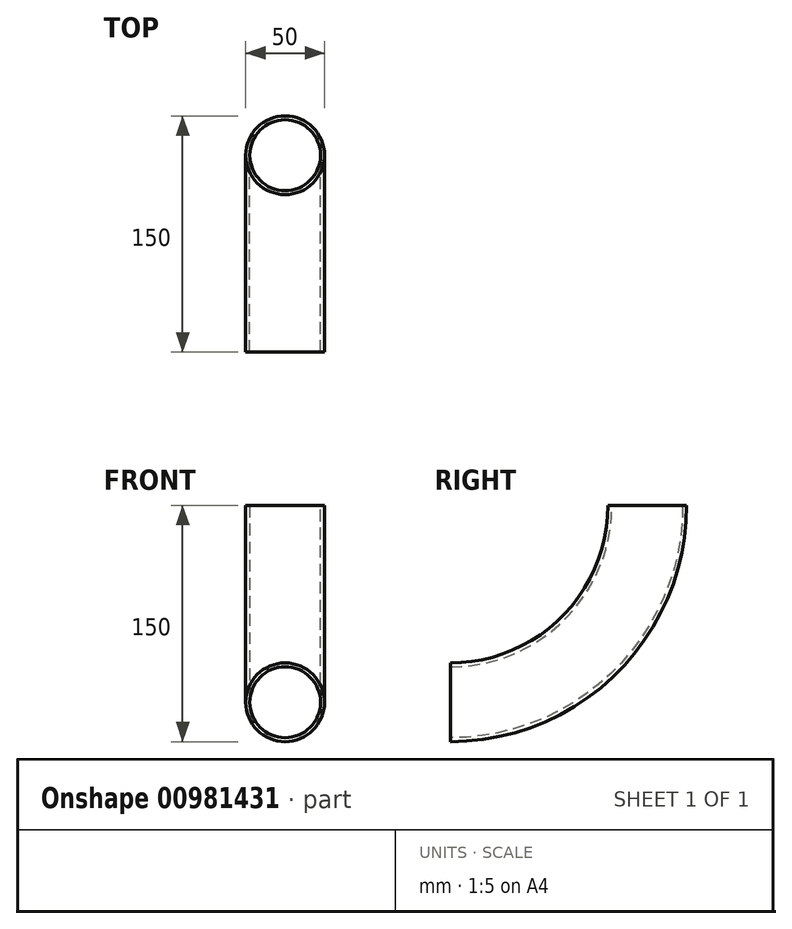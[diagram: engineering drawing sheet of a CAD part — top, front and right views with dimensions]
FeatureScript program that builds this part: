
annotation { "Feature Type Name" : "Feature", "Feature Type Description" : "" }
export const myFeature = defineFeature(function(context is Context, id is Id, definition is map)
    precondition{}
    {
        {
            var Q0;
            Q0=qCreatedBy(makeId("Right.planeOp"),FACE);
            var sketch = newSketch(context, id + "F0", { "sketchPlane" : qUnion([Q0])});
            skArc(sketch, "E0", {"start": v(0, -100) * mm, "mid": v(70.71, -70.71) * mm, "end": v(100, 0) * mm});
            skArc(sketch, "E1.0", {"start": v(0, -150) * mm, "mid": v(106.07, -106.07) * mm, "end": v(150, 0) * mm});
            skLineSegment(sketch, "E2", {"start": v(100, 0) * mm, "end": v(150, 0) * mm});
            skLineSegment(sketch, "E3", {"start": v(0, -100) * mm, "end": v(0, -150) * mm});
            skSolve(sketch);
        }
        {
            var Q0;
            Q0=makeQuery(id+"F0.imprint","IMPRINT",FACE,{"disambiguationData":[TD([[makeQuery(id+"F0.imprint","IMPRINT",EDGE,{"derivedFrom":sQuery(id+"F0.wireOp",EDGE,"E0")}),-1.0]])]});
            extrude(context, id + "F1", {"entities" : qUnion([Q0]), "endBound" : BoundingType.SYMMETRIC, "depth" : 50 * mm, "offsetDistance" : 25 * mm});
        }
        {
            var Q0;
            Q0=makeQuery(id+"F1.opExtrude","CAP_EDGE",EDGE,{"disambiguationData":[OSD([sQuery(id+"F0.wireOp",EDGE,"E0")])],"isStart":false});
            var Q1;
            Q1=makeQuery(id+"F1.opExtrude","CAP_EDGE",EDGE,{"disambiguationData":[OSD([sQuery(id+"F0.wireOp",EDGE,"E1.0")])],"isStart":false});
            var Q2;
            Q2=makeQuery(id+"F1.opExtrude","CAP_EDGE",EDGE,{"disambiguationData":[OSD([sQuery(id+"F0.wireOp",EDGE,"E1.0")])],"isStart":true});
            var Q3;
            Q3=makeQuery(id+"F1.opExtrude","CAP_EDGE",EDGE,{"disambiguationData":[OSD([sQuery(id+"F0.wireOp",EDGE,"E0")])],"isStart":true});
            fillet(context, id + "F2", {"entities" : qUnion([Q0, Q1, Q2, Q3]), "radius" : 25 * mm, "tangentPropagation" : true, "allowEdgeOverflow" : false});
        }
        {
            var Q0;
            Q0=makeQuery(id+"F1.opExtrude","SWEPT_FACE",FACE,{"disambiguationData":[OSD([sQuery(id+"F0.wireOp",EDGE,"E2")])]});
            var Q1;
            Q1=makeQuery(id+"F1.opExtrude","SWEPT_FACE",FACE,{"disambiguationData":[OSD([sQuery(id+"F0.wireOp",EDGE,"E3")])]});
            shell(context, id + "F3", {"entities" : qUnion([Q0, Q1]), "thickness" : 2.5 * mm});
        }
    });
